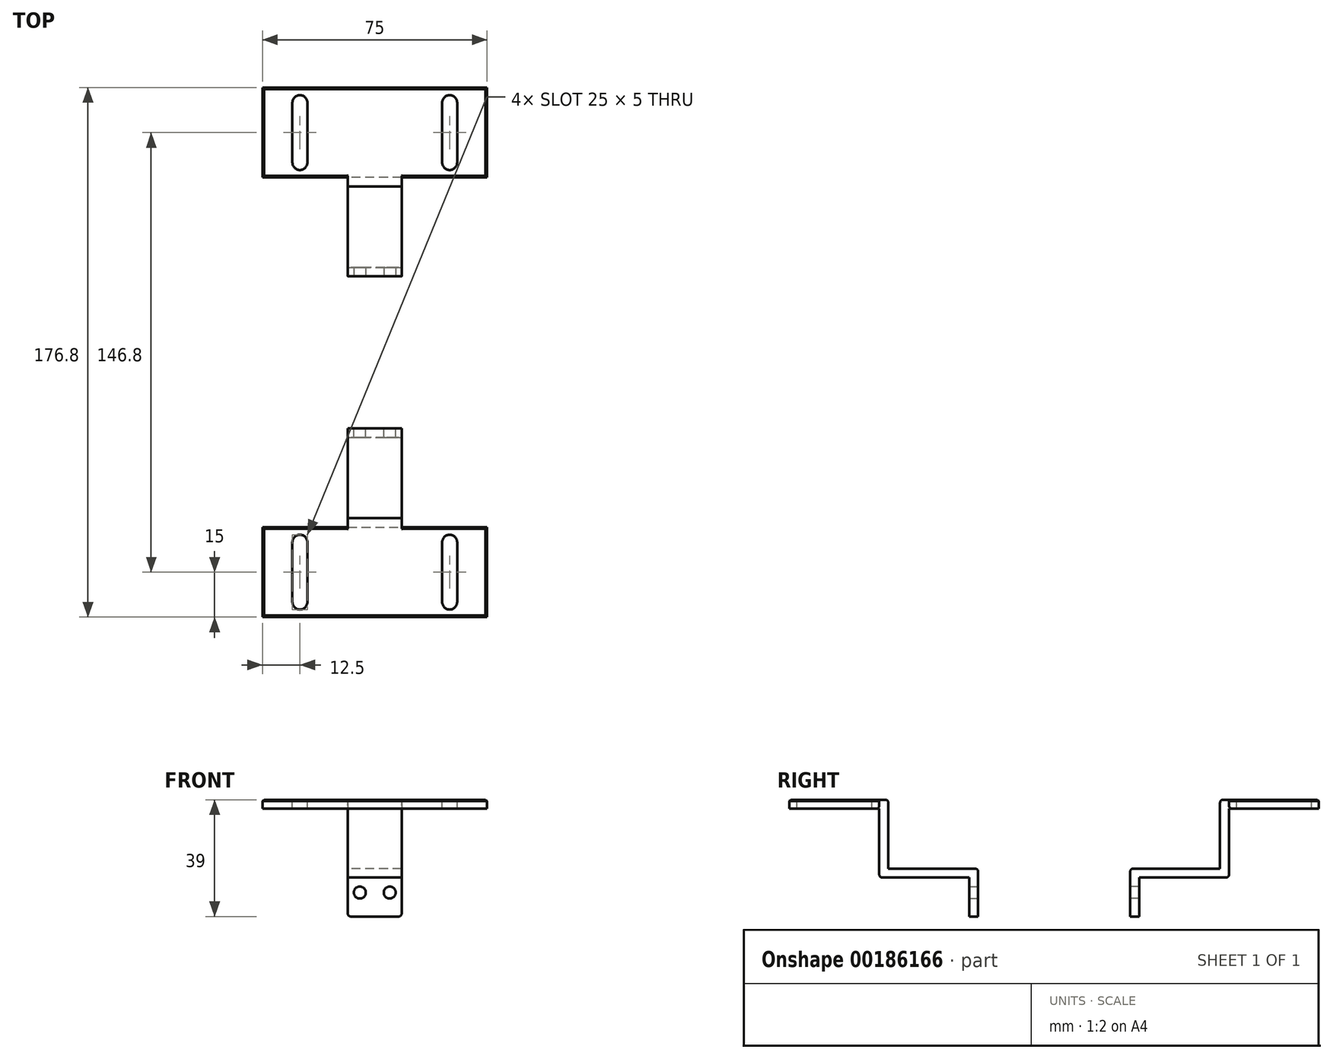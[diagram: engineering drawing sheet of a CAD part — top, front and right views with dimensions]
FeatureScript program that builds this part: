
annotation { "Feature Type Name" : "Feature", "Feature Type Description" : "" }
export const myFeature = defineFeature(function(context is Context, id is Id, definition is map)
    precondition{}
    {
        {
            var Q0;
            Q0=qCreatedBy(makeId("Front.planeOp"),FACE);
            var sketch = newSketch(context, id + "F0", { "sketchPlane" : qUnion([Q0])});
            skLineSegment(sketch, "E0.bottom", {"start": v(9, -8) * mm, "end": v(-9, -8) * mm});
            skLineSegment(sketch, "E0.top", {"start": v(9, 8) * mm, "end": v(-9, 8) * mm});
            skLineSegment(sketch, "E0.left", {"start": v(9, -8) * mm, "end": v(9, 8) * mm});
            skLineSegment(sketch, "E0.right", {"start": v(-9, -8) * mm, "end": v(-9, 8) * mm});
            skPoint(sketch, "E0.middle", {"position": v(0, 0) * mm});
            skLineSegment(sketch, "E1", {"start": v(0, 8) * mm, "end": v(0, -8) * mm});
            skCircle(sketch, "E2", {"center": v(-5, 0) * mm, "radius": 2 * mm});
            skCircle(sketch, "E3.MirrorC", {"center": v(5, 0) * mm, "radius": 2 * mm});
            skSolve(sketch);
        }
        {
            var Q0;
            {var subQ1=sQuery(id+"F0.wireOp",EDGE,"E0.left");Q0=makeQuery(id+"F0.imprint","IMPRINT",FACE,{"disambiguationData":[TD([[makeQuery(id+"F0.imprint","IMPRINT",EDGE,{"derivedFrom":subQ1}),1.0]])]});}
            var Q1;
            {var subQ1=sQuery(id+"F0.wireOp",EDGE,"E0.right");Q1=makeQuery(id+"F0.imprint","IMPRINT",FACE,{"disambiguationData":[TD([[makeQuery(id+"F0.imprint","IMPRINT",EDGE,{"derivedFrom":subQ1}),-1.0]])]});}
            extrude(context, id + "F1", {"entities" : qUnion([Q0, Q1]), "depth" : 3 * mm});
        }
        {
            var Q0;
            Q0=makeQuery(id+"F1.opExtrude","CAP_FACE",FACE,{"disambiguationData":[OSD([sQuery(id+"F0.wireOp",EDGE,"E0.bottom"),sQuery(id+"F0.wireOp",EDGE,"E0.top"),sQuery(id+"F0.wireOp",EDGE,"E0.left"),sQuery(id+"F0.wireOp",EDGE,"E0.right"),sQuery(id+"F0.wireOp",EDGE,"E2"),sQuery(id+"F0.wireOp",EDGE,"E3.MirrorC")])],"isStart":false});
            var sketch = newSketch(context, id + "F2", { "sketchPlane" : qUnion([Q0])});
            skLineSegment(sketch, "E4.bottom", {"start": v(-9, 8) * mm, "end": v(9, 8) * mm});
            skLineSegment(sketch, "E4.top", {"start": v(-9, 5) * mm, "end": v(9, 5) * mm});
            skLineSegment(sketch, "E4.left", {"start": v(-9, 8) * mm, "end": v(-9, 5) * mm});
            skLineSegment(sketch, "E4.right", {"start": v(9, 8) * mm, "end": v(9, 5) * mm});
            skSolve(sketch);
        }
        {
            var Q0;
            Q0=makeQuery(id+"F2.imprint","IMPRINT",FACE,{"disambiguationData":[TD([[makeQuery(id+"F2.imprint","IMPRINT",EDGE,{"derivedFrom":sQuery(id+"F2.wireOp",EDGE,"E4.bottom")}),1.0]])]});
            extrude(context, id + "F3", {"entities" : qUnion([Q0]), "operationType" : NewBodyOperationType.ADD, "depth" : 30 * mm});
        }
        {
            var Q0;
            Q0=makeQuery(id+"F3.boolean.opBoolean","MERGE",FACE,{"derivedFrom":[makeQuery(id+"F1.opExtrude","SWEPT_FACE",FACE,{"disambiguationData":[OSD([sQuery(id+"F0.wireOp",EDGE,"E0.top")])]}),makeQuery(id+"F3.opExtrude","SWEPT_FACE",FACE,{"disambiguationData":[OSD([sQuery(id+"F2.wireOp",EDGE,"E4.bottom")])]})]});
            var sketch = newSketch(context, id + "F4", { "sketchPlane" : qUnion([Q0])});
            skLineSegment(sketch, "E5.bottom", {"start": v(-9, -33) * mm, "end": v(9, -33) * mm});
            skLineSegment(sketch, "E5.top", {"start": v(-9, -30) * mm, "end": v(9, -30) * mm});
            skLineSegment(sketch, "E5.left", {"start": v(-9, -33) * mm, "end": v(-9, -30) * mm});
            skLineSegment(sketch, "E5.right", {"start": v(9, -33) * mm, "end": v(9, -30) * mm});
            skSolve(sketch);
        }
        {
            var Q0;
            Q0=makeQuery(id+"F4.imprint","IMPRINT",FACE,{"disambiguationData":[TD([[makeQuery(id+"F4.imprint","IMPRINT",EDGE,{"derivedFrom":sQuery(id+"F4.wireOp",EDGE,"E5.bottom")}),-1.0]])]});
            extrude(context, id + "F5", {"entities" : qUnion([Q0]), "operationType" : NewBodyOperationType.ADD, "depth" : 23 * mm});
        }
        {
            var Q0;
            Q0=makeQuery(id+"F5.boolean.opBoolean","MERGE",FACE,{"derivedFrom":[makeQuery(id+"F3.opExtrude","CAP_FACE",FACE,{"disambiguationData":[OSD([sQuery(id+"F2.wireOp",EDGE,"E4.bottom"),sQuery(id+"F2.wireOp",EDGE,"E4.top"),sQuery(id+"F2.wireOp",EDGE,"E4.left"),sQuery(id+"F2.wireOp",EDGE,"E4.right")])],"isStart":false}),makeQuery(id+"F5.opExtrude","SWEPT_FACE",FACE,{"disambiguationData":[OSD([sQuery(id+"F4.wireOp",EDGE,"E5.bottom")])]})]});
            var sketch = newSketch(context, id + "F6", { "sketchPlane" : qUnion([Q0])});
            skLineSegment(sketch, "E6.bottom", {"start": v(37.5, 28) * mm, "end": v(-37.5, 28) * mm});
            skLineSegment(sketch, "E6.top", {"start": v(37.5, 31) * mm, "end": v(-37.5, 31) * mm});
            skLineSegment(sketch, "E6.left", {"start": v(37.5, 28) * mm, "end": v(37.5, 31) * mm});
            skLineSegment(sketch, "E6.right", {"start": v(-37.5, 28) * mm, "end": v(-37.5, 31) * mm});
            skPoint(sketch, "E6.middle", {"position": v(0, 29.5) * mm});
            skPoint(sketch, "E6.middle.positionSnap0", {"position": v(0, 31) * mm});
            skPoint(sketch, "E6.centerSnap0", {"position": v(0, 31) * mm});
            skSolve(sketch);
        }
        {
            var Q0;
            {var subQ0=sQuery(id+"F6.wireOp",EDGE,"E6.right");Q0=makeQuery(id+"F6.imprint","IMPRINT",FACE,{"disambiguationData":[TD([[makeQuery(id+"F6.imprint","IMPRINT",EDGE,{"derivedFrom":subQ0}),-1.0]])]});}
            var Q1;
            {var subQ0=sQuery(id+"F6.wireOp",EDGE,"E6.bottom");var subQ1=sQuery(id+"F4.wireOp",EDGE,"E5.bottom");var subQ2=makeQuery(id+"F5.boolean.opBoolean","MERGE",EDGE,{"derivedFrom":[makeQuery(id+"F3.opExtrude","CAP_EDGE",EDGE,{"disambiguationData":[OSD([sQuery(id+"F2.wireOp",EDGE,"E4.right")])],"isStart":false}),makeQuery(id+"F5.opExtrude","SWEPT_EDGE",EDGE,{"disambiguationData":[OSD([subQ1,sQuery(id+"F4.wireOp",EDGE,"E5.right")])]})]});var subQ3=makeQuery(id+"F6.imprint","INTERSECT",VERTEX,{"derivedFrom":[subQ2,subQ0]});Q1=makeQuery(id+"F6.imprint","IMPRINT",FACE,{"disambiguationData":[TD([[makeQuery(id+"F6.imprint","IMPRINT",EDGE,{"disambiguationData":[TD([[subQ3,-1.0]])],"derivedFrom":subQ0}),-1.0]])]});}
            var Q2;
            {var subQ0=sQuery(id+"F6.wireOp",EDGE,"E6.left");Q2=makeQuery(id+"F6.imprint","IMPRINT",FACE,{"disambiguationData":[TD([[makeQuery(id+"F6.imprint","IMPRINT",EDGE,{"derivedFrom":subQ0}),1.0]])]});}
            extrude(context, id + "F7", {"entities" : qUnion([Q0, Q1, Q2]), "operationType" : NewBodyOperationType.ADD, "depth" : 30 * mm});
        }
        {
            var Q0;
            Q0=makeQuery(id+"F7.boolean.opBoolean","MERGE",FACE,{"derivedFrom":[makeQuery(id+"F5.opExtrude","CAP_FACE",FACE,{"disambiguationData":[OSD([sQuery(id+"F4.wireOp",EDGE,"E5.bottom"),sQuery(id+"F4.wireOp",EDGE,"E5.top"),sQuery(id+"F4.wireOp",EDGE,"E5.left"),sQuery(id+"F4.wireOp",EDGE,"E5.right")])],"isStart":false}),makeQuery(id+"F7.opExtrude","SWEPT_FACE",FACE,{"disambiguationData":[OSD([sQuery(id+"F6.wireOp",EDGE,"E6.top")])]})]});
            var sketch = newSketch(context, id + "F8", { "sketchPlane" : qUnion([Q0])});
            skLineSegment(sketch, "E7.bottom", {"start": v(-22.5, -58) * mm, "end": v(-27.5, -58) * mm});
            skLineSegment(sketch, "E7.top", {"start": v(-22.5, -38) * mm, "end": v(-27.5, -38) * mm});
            skLineSegment(sketch, "E7.left", {"start": v(-22.5, -58) * mm, "end": v(-22.5, -38) * mm});
            skLineSegment(sketch, "E7.right", {"start": v(-27.5, -58) * mm, "end": v(-27.5, -38) * mm});
            skPoint(sketch, "E7.middle", {"position": v(-25, -48) * mm});
            skLineSegment(sketch, "E8", {"start": v(0, -30) * mm, "end": v(0, -63) * mm});
            skLineSegment(sketch, "E9.MirrorCS", {"start": v(22.5, -58) * mm, "end": v(22.5, -38) * mm});
            skLineSegment(sketch, "E10.MirrorCS", {"start": v(22.5, -38) * mm, "end": v(27.5, -38) * mm});
            skLineSegment(sketch, "E11.MirrorCS", {"start": v(27.5, -58) * mm, "end": v(27.5, -38) * mm});
            skLineSegment(sketch, "E12.MirrorCS", {"start": v(22.5, -58) * mm, "end": v(27.5, -58) * mm});
            skArc(sketch, "E13", {"start": v(-27.5, -38) * mm, "mid": v(-25, -35.5) * mm, "end": v(-22.5, -38) * mm});
            skArc(sketch, "E14", {"start": v(-27.5, -58) * mm, "mid": v(-25, -60.5) * mm, "end": v(-22.5, -58) * mm});
            skArc(sketch, "E15", {"start": v(22.5, -58) * mm, "mid": v(25, -60.5) * mm, "end": v(27.5, -58) * mm});
            skArc(sketch, "E16", {"start": v(27.5, -38) * mm, "mid": v(25, -35.5) * mm, "end": v(22.5, -38) * mm});
            skSolve(sketch);
        }
        {
            var Q0;
            Q0=makeQuery(id+"F8.imprint","IMPRINT",FACE,{"disambiguationData":[TD([[makeQuery(id+"F8.imprint","IMPRINT",EDGE,{"derivedFrom":sQuery(id+"F8.wireOp",EDGE,"E7.top")}),-1.0]])]});
            var Q1;
            Q1=makeQuery(id+"F8.imprint","IMPRINT",FACE,{"disambiguationData":[TD([[makeQuery(id+"F8.imprint","IMPRINT",EDGE,{"derivedFrom":sQuery(id+"F8.wireOp",EDGE,"E7.bottom")}),-1.0]])]});
            var Q2;
            Q2=makeQuery(id+"F8.imprint","IMPRINT",FACE,{"disambiguationData":[TD([[makeQuery(id+"F8.imprint","IMPRINT",EDGE,{"derivedFrom":sQuery(id+"F8.wireOp",EDGE,"E12.MirrorCS")}),-1.0]])]});
            var Q3;
            Q3=makeQuery(id+"F8.imprint","IMPRINT",FACE,{"disambiguationData":[TD([[makeQuery(id+"F8.imprint","IMPRINT",EDGE,{"derivedFrom":sQuery(id+"F8.wireOp",EDGE,"E9.MirrorCS")}),-1.0]])]});
            var Q4;
            Q4=makeQuery(id+"F8.imprint","IMPRINT",FACE,{"disambiguationData":[TD([[makeQuery(id+"F8.imprint","IMPRINT",EDGE,{"derivedFrom":sQuery(id+"F8.wireOp",EDGE,"E7.bottom")}),1.0]])]});
            var Q5;
            Q5=makeQuery(id+"F8.imprint","IMPRINT",FACE,{"disambiguationData":[TD([[makeQuery(id+"F8.imprint","IMPRINT",EDGE,{"derivedFrom":sQuery(id+"F8.wireOp",EDGE,"E10.MirrorCS")}),1.0]])]});
            extrude(context, id + "F9", {"entities" : qUnion([Q0, Q1, Q2, Q3, Q4, Q5]), "operationType" : NewBodyOperationType.REMOVE, "endBound" : BoundingType.THROUGH_ALL, "oppositeDirection" : true, "depth" : 25.4 * mm});
        }
        {
            var Q0;
            Q0=makeQuery(id+"F1.opExtrude","CAP_EDGE",EDGE,{"disambiguationData":[OSD([sQuery(id+"F0.wireOp",EDGE,"E0.top")])],"isStart":true});
            var Q1;
            Q1=makeQuery(id+"F5.opExtrude","CAP_EDGE",EDGE,{"disambiguationData":[OSD([sQuery(id+"F4.wireOp",EDGE,"E5.top")])],"isStart":true});
            var Q2;
            Q2=makeQuery(id+"F5.opExtrude","CAP_EDGE",EDGE,{"disambiguationData":[OSD([sQuery(id+"F4.wireOp",EDGE,"E5.top")])],"isStart":false});
            fillet(context, id + "F10", {"entities" : qUnion([Q0, Q1, Q2]), "radius" : 1 * mm, "tangentPropagation" : true, "allowEdgeOverflow" : false});
        }
        {
            var Q0;
            Q0=makeQuery(id+"F3.opExtrude","CAP_EDGE",EDGE,{"disambiguationData":[OSD([sQuery(id+"F2.wireOp",EDGE,"E4.top")])],"isStart":true});
            var Q1;
            Q1=makeQuery(id+"F3.opExtrude","CAP_EDGE",EDGE,{"disambiguationData":[OSD([sQuery(id+"F2.wireOp",EDGE,"E4.top")])],"isStart":false});
            var Q2;
            {var subQ0=sQuery(id+"F2.wireOp",EDGE,"E4.right");var subQ1=sQuery(id+"F2.wireOp",EDGE,"E4.left");var subQ2=sQuery(id+"F6.wireOp",EDGE,"E6.bottom");Q2=makeQuery(id+"F7.boolean.opBoolean","SPLIT",EDGE,{"disambiguationData":[TD([makeQuery(id+"F1.opExtrude","SWEPT_FACE",FACE,{"disambiguationData":[OSD([sQuery(id+"F0.wireOp",EDGE,"E0.left")])]}),makeQuery(id+"F1.opExtrude","SWEPT_FACE",FACE,{"disambiguationData":[OSD([sQuery(id+"F0.wireOp",EDGE,"E0.right")])]}),makeQuery(id+"F3.opExtrude","CAP_FACE",FACE,{"disambiguationData":[OSD([sQuery(id+"F2.wireOp",EDGE,"E4.bottom"),sQuery(id+"F2.wireOp",EDGE,"E4.top"),subQ1,subQ0])],"isStart":false}),makeQuery(id+"F3.opExtrude","SWEPT_FACE",FACE,{"disambiguationData":[OSD([subQ1])]}),makeQuery(id+"F3.opExtrude","SWEPT_FACE",FACE,{"disambiguationData":[OSD([subQ0])]}),makeQuery(id+"F5.opExtrude","SWEPT_FACE",FACE,{"disambiguationData":[OSD([sQuery(id+"F4.wireOp",EDGE,"E5.bottom")])]}),makeQuery(id+"F5.opExtrude","SWEPT_FACE",FACE,{"disambiguationData":[OSD([sQuery(id+"F4.wireOp",EDGE,"E5.left")])]}),makeQuery(id+"F5.opExtrude","SWEPT_FACE",FACE,{"disambiguationData":[OSD([sQuery(id+"F4.wireOp",EDGE,"E5.right")])]}),makeQuery(id+"F7.opExtrude","SWEPT_FACE",FACE,{"disambiguationData":[OSD([subQ2])]}),makeQuery(id+"F7.opExtrude","CAP_FACE",FACE,{"disambiguationData":[OSD([subQ2,sQuery(id+"F6.wireOp",EDGE,"E6.top"),sQuery(id+"F6.wireOp",EDGE,"E6.left"),sQuery(id+"F6.wireOp",EDGE,"E6.right")])],"isStart":true})])],"derivedFrom":makeQuery(id+"F7.opExtrude","CAP_EDGE",EDGE,{"disambiguationData":[OSD([subQ2])],"isStart":true})});}
            fillet(context, id + "F11", {"entities" : qUnion([Q0, Q1, Q2]), "radius" : 1 * mm, "tangentPropagation" : true, "allowEdgeOverflow" : false});
        }
        {
            var Q0;
            {var subQ2=sQuery(id+"F6.wireOp",EDGE,"E6.top");Q0=makeQuery(id+"F7.boolean.opBoolean","SPLIT",EDGE,{"disambiguationData":[TD([makeQuery(id+"F1.opExtrude","SWEPT_FACE",FACE,{"disambiguationData":[OSD([sQuery(id+"F0.wireOp",EDGE,"E0.left")])]})])],"derivedFrom":makeQuery(id+"F7.opExtrude","CAP_EDGE",EDGE,{"disambiguationData":[OSD([subQ2])],"isStart":true})});}
            var Q1;
            {var subQ2=sQuery(id+"F6.wireOp",EDGE,"E6.top");Q1=makeQuery(id+"F7.boolean.opBoolean","SPLIT",EDGE,{"disambiguationData":[TD([makeQuery(id+"F1.opExtrude","SWEPT_FACE",FACE,{"disambiguationData":[OSD([sQuery(id+"F0.wireOp",EDGE,"E0.right")])]})])],"derivedFrom":makeQuery(id+"F7.opExtrude","CAP_EDGE",EDGE,{"disambiguationData":[OSD([subQ2])],"isStart":true})});}
            var Q2;
            Q2=makeQuery(id+"F7.opExtrude","SWEPT_EDGE",EDGE,{"disambiguationData":[OSD([sQuery(id+"F6.wireOp",EDGE,"E6.top"),sQuery(id+"F6.wireOp",EDGE,"E6.left")])]});
            var Q3;
            Q3=makeQuery(id+"F7.opExtrude","CAP_EDGE",EDGE,{"disambiguationData":[OSD([sQuery(id+"F6.wireOp",EDGE,"E6.top")])],"isStart":false});
            var Q4;
            Q4=makeQuery(id+"F7.opExtrude","SWEPT_EDGE",EDGE,{"disambiguationData":[OSD([sQuery(id+"F6.wireOp",EDGE,"E6.top"),sQuery(id+"F6.wireOp",EDGE,"E6.right")])]});
            chamfer(context, id + "F12", {"entities" : qUnion([Q0, Q1, Q2, Q3, Q4]), "width" : .5 * mm, "tangentPropagation" : true});
        }
        {
            var Q0;
            Q0=makeQuery(id+"F1.opExtrude","SWEPT_EDGE",EDGE,{"disambiguationData":[OSD([sQuery(id+"F0.wireOp",EDGE,"E0.bottom"),sQuery(id+"F0.wireOp",EDGE,"E0.left")])]});
            var Q1;
            Q1=makeQuery(id+"F1.opExtrude","SWEPT_EDGE",EDGE,{"disambiguationData":[OSD([sQuery(id+"F0.wireOp",EDGE,"E0.bottom"),sQuery(id+"F0.wireOp",EDGE,"E0.right")])]});
            fillet(context, id + "F13", {"entities" : qUnion([Q0, Q1]), "radius" : 1 * mm, "tangentPropagation" : true, "allowEdgeOverflow" : false});
        }
        {
            var Q0;
            Q0=makeQuery(id+"F1.opExtrude","CAP_FACE",FACE,{"disambiguationData":[OSD([sQuery(id+"F0.wireOp",EDGE,"E0.bottom"),sQuery(id+"F0.wireOp",EDGE,"E0.top"),sQuery(id+"F0.wireOp",EDGE,"E0.left"),sQuery(id+"F0.wireOp",EDGE,"E0.right"),sQuery(id+"F0.wireOp",EDGE,"E2"),sQuery(id+"F0.wireOp",EDGE,"E3.MirrorC")])],"isStart":true});
            cPlane(context, id + "F14", {"entities" : qUnion([Q0]), "cplaneType" : CPlaneType.OFFSET, "offset" : 25.4 * mm, "width" : 152.4 * mm, "height" : 152.4 * mm});
        }
        {
            var Q0;
            Q0=makeQuery(id+"F1.opExtrude","SWEPT_BODY",BODY,{"disambiguationData":[OSD([sQuery(id+"F0.wireOp",EDGE,"E0.bottom"),sQuery(id+"F0.wireOp",EDGE,"E0.top"),sQuery(id+"F0.wireOp",EDGE,"E0.left"),sQuery(id+"F0.wireOp",EDGE,"E0.right"),sQuery(id+"F0.wireOp",EDGE,"E2"),sQuery(id+"F0.wireOp",EDGE,"E3.MirrorC")])]});
            var Q1;
            Q1=qCreatedBy(id+"F14.planeOp",FACE);
            mirror(context, id + "F15", {"entities" : qUnion([Q0]), "mirrorPlane" : qUnion([Q1])});
        }
    });
